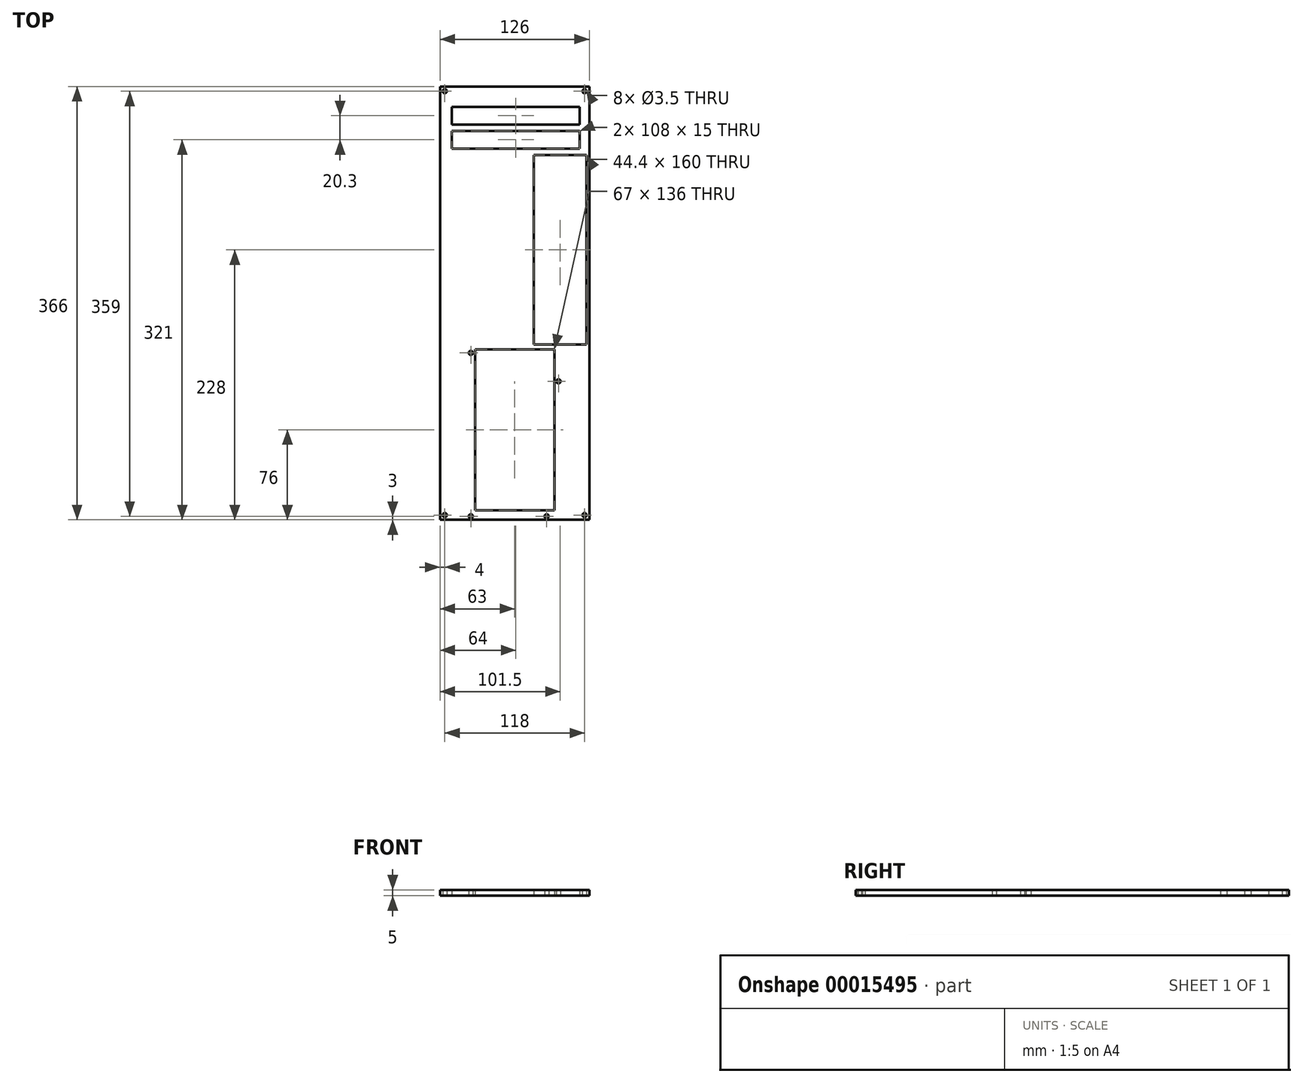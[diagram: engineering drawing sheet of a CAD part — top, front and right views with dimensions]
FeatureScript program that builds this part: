
annotation { "Feature Type Name" : "Feature", "Feature Type Description" : "" }
export const myFeature = defineFeature(function(context is Context, id is Id, definition is map)
    precondition{}
    {
        {
            var Q0;
            Q0=qCreatedBy(makeId("Top.planeOp"),FACE);
            var sketch = newSketch(context, id + "F0", { "sketchPlane" : qUnion([Q0])});
            skLineSegment(sketch, "E0.rect.bottom", {"start": v(63, 183) * mm, "end": v(-63, 183) * mm});
            skLineSegment(sketch, "E0.rect.top", {"start": v(63, -183) * mm, "end": v(-63, -183) * mm});
            skLineSegment(sketch, "E0.rect.left", {"start": v(63, 183) * mm, "end": v(63, -183) * mm});
            skLineSegment(sketch, "E0.rect.right", {"start": v(-63, 183) * mm, "end": v(-63, -183) * mm});
            skPoint(sketch, "E0.rect.middle", {"position": v(0, 0) * mm});
            skSolve(sketch);
        }
        {
            var Q0;
            Q0 = qSketchRegion(id + "F0", true);
            extrude(context, id + "F1", {"entities" : qUnion([Q0]), "depth" : 5 * mm});
        }
        {
            var Q0;
            Q0=qCreatedBy(makeId("Top.planeOp"),FACE);
            var sketch = newSketch(context, id + "F2", { "sketchPlane" : qUnion([Q0])});
            skLineSegment(sketch, "E1.rect.bottom", {"start": v(-59, 179) * mm, "end": v(59, 179) * mm, "construction": true});
            skLineSegment(sketch, "E1.rect.top", {"start": v(-59, -179) * mm, "end": v(59, -179) * mm, "construction": true});
            skLineSegment(sketch, "E1.rect.left", {"start": v(-59, 179) * mm, "end": v(-59, -179) * mm, "construction": true});
            skLineSegment(sketch, "E1.rect.right", {"start": v(59, 179) * mm, "end": v(59, -179) * mm, "construction": true});
            skPoint(sketch, "E1.rect.middle", {"position": v(0, 0) * mm});
            skCircle(sketch, "E2", {"center": v(-59, -179) * mm, "radius": 1.75 * mm});
            skCircle(sketch, "E3", {"center": v(59, -179) * mm, "radius": 1.75 * mm});
            skCircle(sketch, "E4", {"center": v(59, 179) * mm, "radius": 1.75 * mm});
            skCircle(sketch, "E5", {"center": v(-59, 179) * mm, "radius": 1.75 * mm});
            skSolve(sketch);
        }
        {
            var Q0;
            Q0 = qSketchRegion(id + "F2", true);
            extrude(context, id + "F3", {"entities" : qUnion([Q0]), "operationType" : NewBodyOperationType.REMOVE, "endBound" : BoundingType.THROUGH_ALL, "depth" : 25 * mm});
        }
        {
            var Q0;
            Q0=qCreatedBy(makeId("Top.planeOp"),FACE);
            var sketch = newSketch(context, id + "F4", { "sketchPlane" : qUnion([Q0])});
            skLineSegment(sketch, "E6.rect.bottom", {"start": v(55, 165.8) * mm, "end": v(-53, 165.8) * mm});
            skLineSegment(sketch, "E6.rect.top", {"start": v(55, 150.8) * mm, "end": v(-53, 150.8) * mm});
            skLineSegment(sketch, "E6.rect.left", {"start": v(55, 165.8) * mm, "end": v(55, 150.8) * mm});
            skLineSegment(sketch, "E6.rect.right", {"start": v(-53, 165.8) * mm, "end": v(-53, 150.8) * mm});
            skPoint(sketch, "E6.rect.middle", {"position": v(1, 158.3) * mm});
            skLineSegment(sketch, "E7.rect.bottom", {"start": v(55, 145.5) * mm, "end": v(-53, 145.5) * mm});
            skLineSegment(sketch, "E7.rect.top", {"start": v(55, 130.5) * mm, "end": v(-53, 130.5) * mm});
            skLineSegment(sketch, "E7.rect.left", {"start": v(55, 145.5) * mm, "end": v(55, 130.5) * mm});
            skLineSegment(sketch, "E7.rect.right", {"start": v(-53, 145.5) * mm, "end": v(-53, 130.5) * mm});
            skPoint(sketch, "E7.rect.middle", {"position": v(1, 138) * mm});
            skLineSegment(sketch, "E8.rect.bottom", {"start": v(60.7, 125) * mm, "end": v(16.3, 125) * mm});
            skLineSegment(sketch, "E8.rect.top", {"start": v(60.7, -35) * mm, "end": v(16.3, -35) * mm});
            skLineSegment(sketch, "E8.rect.left", {"start": v(60.7, 125) * mm, "end": v(60.7, -35) * mm});
            skLineSegment(sketch, "E8.rect.right", {"start": v(16.3, 125) * mm, "end": v(16.3, -35) * mm});
            skPoint(sketch, "E8.rect.middle", {"position": v(38.5, 45) * mm});
            skLineSegment(sketch, "E9.rect.bottom", {"start": v(33.5, -39) * mm, "end": v(-33.5, -39) * mm});
            skLineSegment(sketch, "E9.rect.top", {"start": v(33.5, -175) * mm, "end": v(-33.5, -175) * mm});
            skLineSegment(sketch, "E9.rect.left", {"start": v(33.5, -39) * mm, "end": v(33.5, -175) * mm});
            skLineSegment(sketch, "E9.rect.right", {"start": v(-33.5, -39) * mm, "end": v(-33.5, -175) * mm});
            skPoint(sketch, "E9.rect.middle", {"position": v(0, -107) * mm});
            skSolve(sketch);
        }
        {
            var Q0;
            Q0 = qSketchRegion(id + "F4", true);
            extrude(context, id + "F5", {"entities" : qUnion([Q0]), "operationType" : NewBodyOperationType.REMOVE, "endBound" : BoundingType.THROUGH_ALL, "depth" : 25 * mm});
        }
        {
            var Q0;
            Q0=qCreatedBy(makeId("Top.planeOp"),FACE);
            var sketch = newSketch(context, id + "F6", { "sketchPlane" : qUnion([Q0])});
            skCircle(sketch, "E10", {"center": v(-37, -42) * mm, "radius": 1.75 * mm});
            skCircle(sketch, "E11", {"center": v(-37, -180) * mm, "radius": 1.75 * mm});
            skCircle(sketch, "E12", {"center": v(27, -180) * mm, "radius": 1.75 * mm});
            skCircle(sketch, "E13", {"center": v(37, -66) * mm, "radius": 1.75 * mm});
            skLineSegment(sketch, "E14", {"start": v(0, 0) * mm, "end": v(0, -107) * mm, "construction": true});
            skLineSegment(sketch, "E15", {"start": v(-37, -180) * mm, "end": v(27, -180) * mm, "construction": true});
            skSolve(sketch);
        }
        {
            var Q0;
            Q0 = qSketchRegion(id + "F6", true);
            extrude(context, id + "F7", {"entities" : qUnion([Q0]), "operationType" : NewBodyOperationType.REMOVE, "endBound" : BoundingType.THROUGH_ALL, "depth" : 25 * mm});
        }
    });
